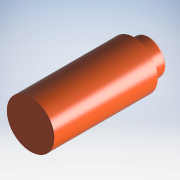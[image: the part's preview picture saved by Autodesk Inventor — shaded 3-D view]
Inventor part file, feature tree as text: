
AUTODESK INVENTOR PART (.ipt)
format: ipt  version: 2018.2 (Build 222227000, 227)  size: 122,368 bytes
history: native  units: mm
features: revolve x1, fillet x1, sketch x1
ambient origin geometry x8: Origin, YZ Plane, XZ Plane, XY Plane, X Axis, Y Axis, Z Axis, Center Point
bodies: Solid1 (feature_tree)
feature tree (3):
  revolve  "Revolution1"  [1 undecoded]
  fillet  "Fillet1"  Radius=2.6mm
  sketch  "Sketch1"  dims[d0=8.0mm d1=5.7mm d2=2.6mm d3=20.0mm d4=90.0deg d5=0.3mm d6=3.3mm d7=8.0mm]
note: 1 required parameter value undecoded (feature->parameter linkage not recoverable at this tier; creation-order binding heuristic only, values carry confidence <= 0.55)
